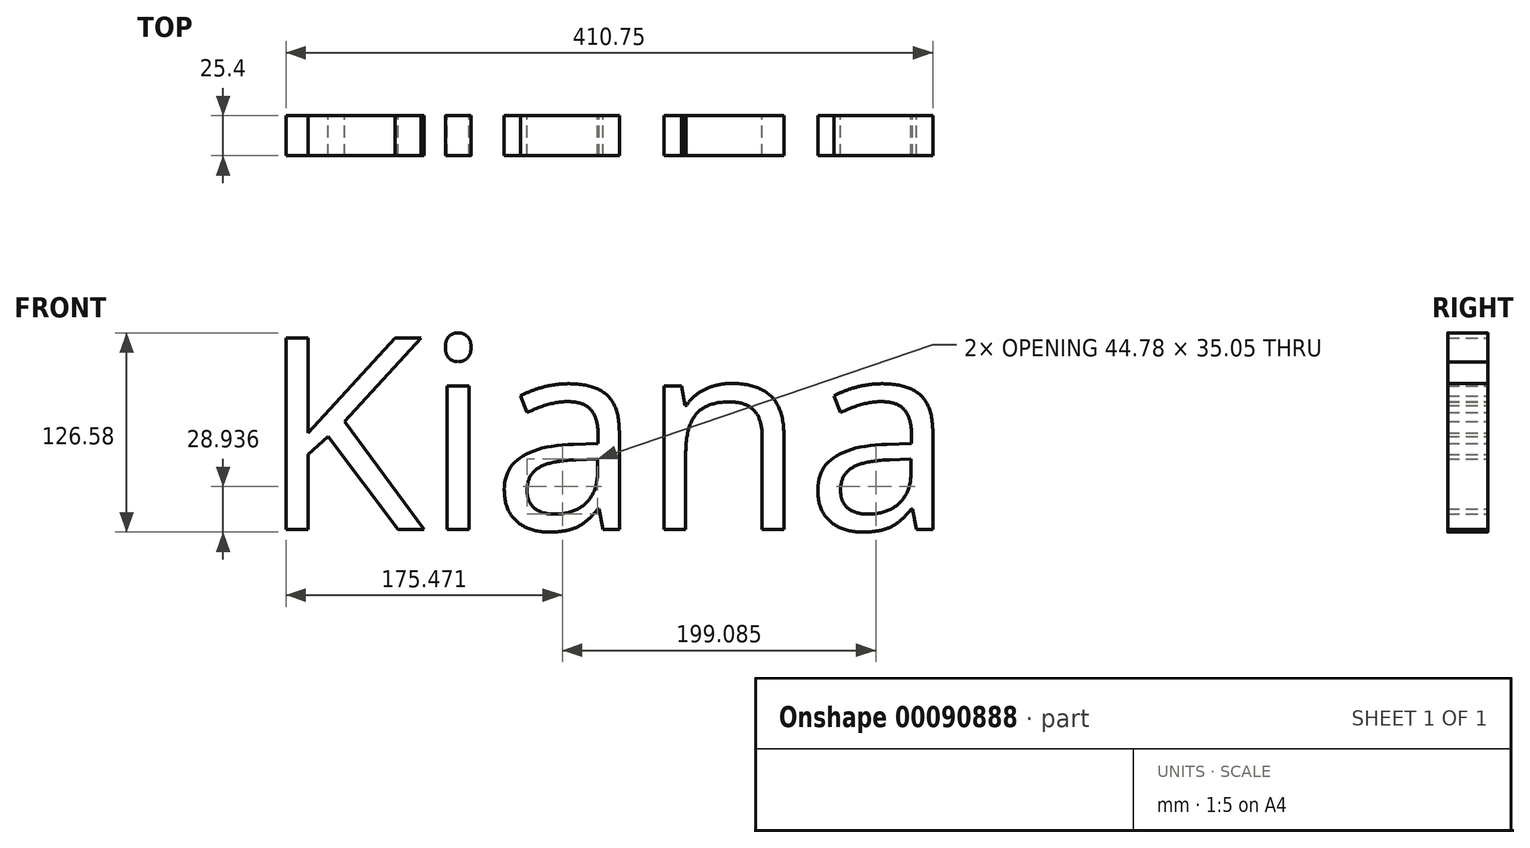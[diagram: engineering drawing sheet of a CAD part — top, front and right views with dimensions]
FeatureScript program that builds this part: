
annotation { "Feature Type Name" : "Feature", "Feature Type Description" : "" }
export const myFeature = defineFeature(function(context is Context, id is Id, definition is map)
    precondition{}
    {
        {
            var Q0;
            Q0=qCreatedBy(makeId("Front.planeOp"),FACE);
            var sketch = newSketch(context, id + "F0", { "sketchPlane" : qUnion([Q0])});
            skText(sketch, "E0", { "text": "Kiana ", "fontName": "OpenSans-Regular.ttf"});
            const initialGuessF0  = {"E0": [-0.07415, -0.05916, 1, 0, 0.12253]};
            skSetInitialGuess(sketch, initialGuessF0);
            skSolve(sketch);
        }
        {
            var Q0;
            Q0 = qSketchRegion(id + "F0", true);
            extrude(context, id + "F1", {"entities" : qUnion([Q0]), "depth" : 25.4 * mm});
        }
    });
